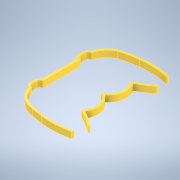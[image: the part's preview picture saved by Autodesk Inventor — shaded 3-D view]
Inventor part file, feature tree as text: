
AUTODESK INVENTOR PART (.ipt)
format: ipt  version: 2022 (Build 260153000, 153)  size: 325,632 bytes
history: native  units: mm
features: sketch x2, extrude x1
ambient origin geometry x8: Origin, YZ Plane, XZ Plane, XY Plane, X Axis, Y Axis, Z Axis, Center Point
bodies: Solid1 (feature_tree)
feature tree (3):
  sketch  "Sketch1"  dims[d0=35.0mm d1=60.0mm]
  extrude  "Extrusion1"  Depth=60.0mm
  sketch  "Sketch2"  dims[d2=17.5mm d3=25.0mm d4=22.5mm d6=25.0mm d7=27.0mm d8=34.0mm d9=27.0mm d10=7.5mm d11=25.0mm d12=27.0mm d13=34.0mm d14=27.0mm d15=6.0mm d16=6.0mm d17=6.0mm d18=6.5mm d22=6.0mm d23=40.0mm d25=360.0deg d27=25.0mm d28=27.0mm d31=40.0mm d32=25.0mm d33=27.0mm d34=5.0mm d35=8.0mm d36=8.0mm d37=35.0mm d38=8.0mm d39=12.0mm d40=8.0mm d41=60.0mm d42=17.5mm d47=4.0mm d48=7.5mm d49=22.5mm d50=25.0mm d51=27.0mm d52=34.0mm d53=6.5mm d54=3.0mm d55=3.0mm d56=6.0mm d57=6.0mm d58=40.0mm d60=360.0deg d62=50.0mm d63=10.0mm d64=0.0mm d65=1.5mm d66=12.5mm d67=27.0mm d68=25.0mm d69=1.401mm d70=13.425896mm d71=200.0mm d72=37.3mm d73=4.0mm d74=37.3mm d75=15.0mm d76=15.0mm d77=30.0mm d78=30.0mm d79=48.0mm d80=9.0mm d81=9.0mm d82=3.0mm d83=3.0mm d84=3.0mm d85=3.0mm d86=6.5mm d87=14.0mm d88=3.0mm d89=1.5mm d90=1.5mm d91=3.0mm d92=3.0mm d93=3.0mm d94=3.0mm d95=3.0mm d96=3.0mm]
